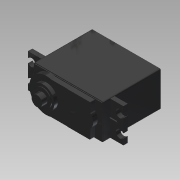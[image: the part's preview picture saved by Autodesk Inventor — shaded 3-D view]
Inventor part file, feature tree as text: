
AUTODESK INVENTOR PART (.ipt)
format: ipt  version: 2015 SP1 (Build 190203100, 203)  size: 403,968 bytes
history: native  units: in
note: dims shown in document units (in); Inventor stores cm internally (conversion verified against a paired STEP export)
features: projected_geometry x7, other x3, sketch x3, imported_body x2
ambient origin geometry x8: Origin, YZ Plane, XZ Plane, XY Plane, X Axis, Y Axis, Z Axis, Center Point
bodies: Body1 (feature_tree), Body2 (feature_tree)
feature tree (15):
  other  "Boss-Extrude1"
  other  "servo1"
  sketch  "Sketch2"  dims[d4=0.0875in]
  sketch  "Sketch4"  dims[d5=0.386in]
  sketch  "Sketch5"  dims[d6=1.937in d7=0.775in d8=0.6725in]
  other  "Boss-Extrude3"
  imported_body  "Base1"
  imported_body  "Base2"
  projected_geometry  "Projected Loop2"
  projected_geometry  "Projected Loop3"
  projected_geometry  "Projected Loop4"
  projected_geometry  "Projected Loop5"
  projected_geometry  "Projected Loop6"
  projected_geometry  "Projected Loop7"
  projected_geometry  "Projected Loop8"
